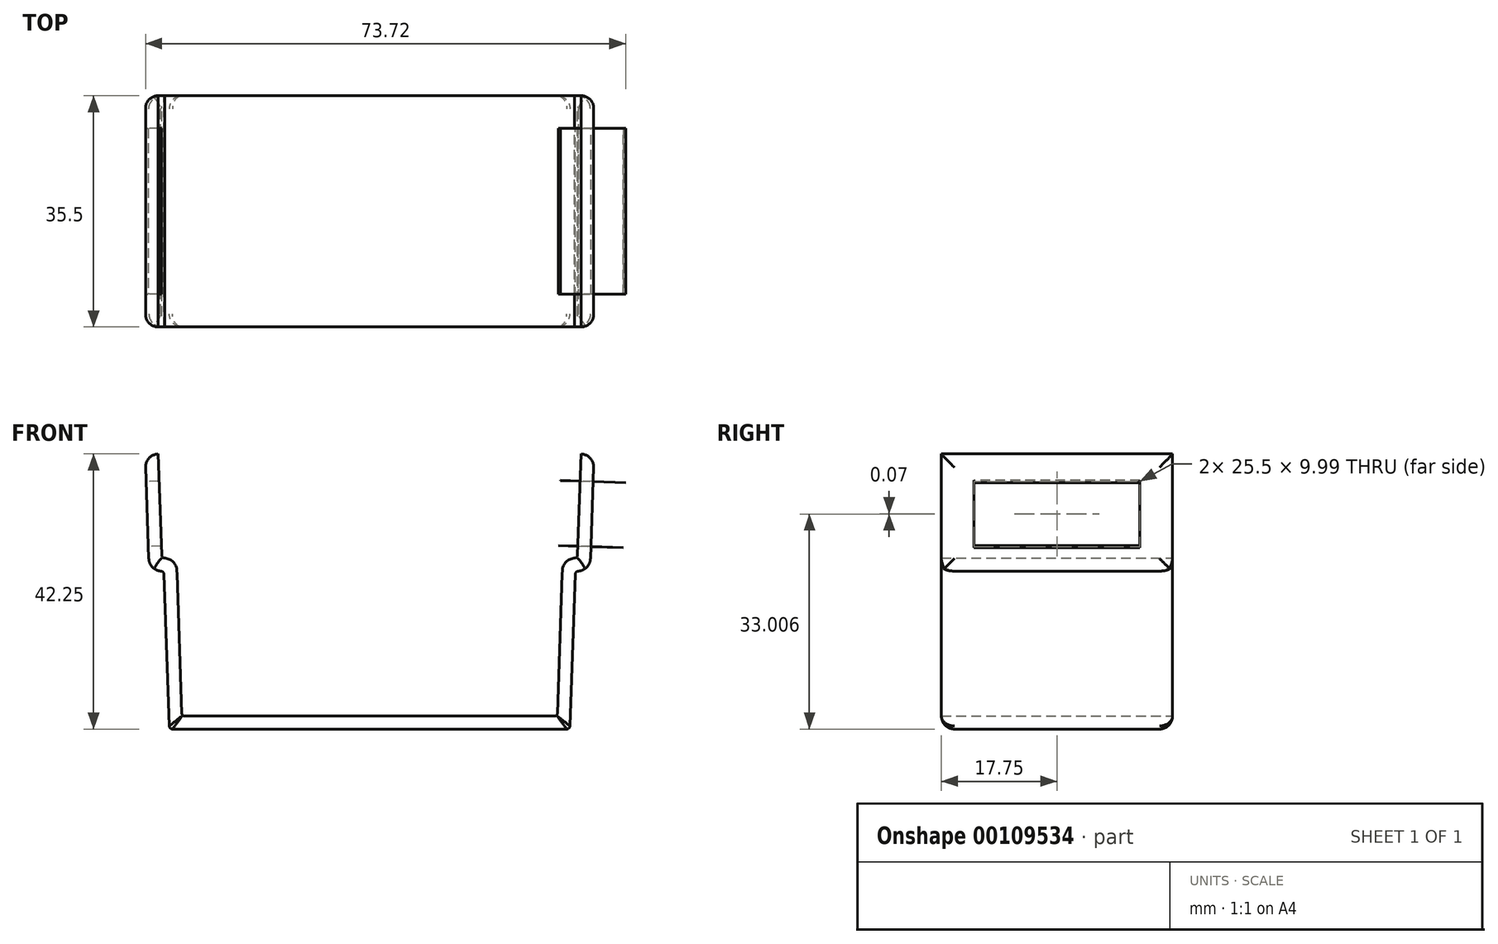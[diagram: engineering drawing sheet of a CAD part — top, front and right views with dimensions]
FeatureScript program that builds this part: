
annotation { "Feature Type Name" : "Feature", "Feature Type Description" : "" }
export const myFeature = defineFeature(function(context is Context, id is Id, definition is map)
    precondition{}
    {
        {
            var Q0;
            Q0=qCreatedBy(makeId("Front.planeOp"),FACE);
            var sketch = newSketch(context, id + "F0", { "sketchPlane" : qUnion([Q0])});
            skLineSegment(sketch, "E0", {"start": v(0, 0) * mm, "end": v(0, -5.67) * mm, "construction": true});
            skLineSegment(sketch, "E1", {"start": v(0, -5.67) * mm, "end": v(34.5, -5.67) * mm, "construction": true});
            skLineSegment(sketch, "E2", {"start": v(34.5, -5.67) * mm, "end": v(34.5, 0) * mm, "construction": true});
            skLineSegment(sketch, "E3.2", {"start": v(0, 2) * mm, "end": v(28.43, 2) * mm});
            skLineSegment(sketch, "E4.MirrorCS", {"start": v(-34.5, -5.67) * mm, "end": v(-34.5, 0) * mm, "construction": true});
            skLineSegment(sketch, "E5.MirrorCS", {"start": v(0, -5.67) * mm, "end": v(-34.5, -5.67) * mm, "construction": true});
            skLineSegment(sketch, "E6", {"start": v(29.6, 24.32) * mm, "end": v(28.83, 2.39) * mm});
            skLineSegment(sketch, "E7", {"start": v(30.77, 0.48) * mm, "end": v(31.58, 23.77) * mm});
            skLineSegment(sketch, "E8", {"start": v(0, 0) * mm, "end": v(30.27, 0) * mm});
            skLineSegment(sketch, "E9", {"start": v(32.23, 42.25) * mm, "end": v(57.13, 42.25) * mm, "construction": true});
            skLineSegment(sketch, "E10", {"start": v(57.13, 42.25) * mm, "end": v(57.13, 26.25) * mm, "construction": true});
            skLineSegment(sketch, "E11", {"start": v(57.13, 26.25) * mm, "end": v(31.92, 26.25) * mm, "construction": true});
            skLineSegment(sketch, "E12", {"start": v(32.08, 24.25) * mm, "end": v(31.92, 24.25) * mm});
            skLineSegment(sketch, "E13", {"start": v(33.91, 26.18) * mm, "end": v(34.48, 42.25) * mm});
            skLineSegment(sketch, "E14", {"start": v(31.43, 26.25) * mm, "end": v(31.6, 26.25) * mm});
            skLineSegment(sketch, "E15", {"start": v(31.93, 26.73) * mm, "end": v(32.47, 42.25) * mm});
            skLineSegment(sketch, "E16", {"start": v(32.47, 42.25) * mm, "end": v(34.48, 42.25) * mm});
            skLineSegment(sketch, "E17.trimOffspring", {"start": v(33.85, 24.25) * mm, "end": v(57.53, 24.25) * mm, "construction": true});
            skPoint(sketch, "E18.visualSharp", {"position": v(29.67, 26.25) * mm});
            skArc(sketch, "E18.filletArc", {"start": v(31.6, 26.25) * mm, "mid": v(30.2, 25.69) * mm, "end": v(29.6, 24.32) * mm});
            skArc(sketch, "E19.filletArc", {"start": v(32.08, 24.25) * mm, "mid": v(31.73, 24.1) * mm, "end": v(31.58, 23.77) * mm});
            skPoint(sketch, "E20.visualSharp", {"position": v(33.85, 24.25) * mm});
            skArc(sketch, "E20.filletArc", {"start": v(31.92, 24.25) * mm, "mid": v(33.3, 24.81) * mm, "end": v(33.91, 26.18) * mm});
            skArc(sketch, "E21.filletArc", {"start": v(31.43, 26.25) * mm, "mid": v(31.78, 26.4) * mm, "end": v(31.93, 26.73) * mm});
            skPoint(sketch, "E22.visualSharp", {"position": v(30.75, 0) * mm});
            skArc(sketch, "E22.filletArc", {"start": v(30.27, 0) * mm, "mid": v(30.61, 0.14) * mm, "end": v(30.77, 0.48) * mm});
            skPoint(sketch, "E23.visualSharp", {"position": v(28.82, 2) * mm});
            skArc(sketch, "E23.filletArc", {"start": v(28.43, 2) * mm, "mid": v(28.71, 2.11) * mm, "end": v(28.83, 2.39) * mm});
            skLineSegment(sketch, "E24.MirrorCS", {"start": v(-32.08, 24.25) * mm, "end": v(-31.92, 24.25) * mm});
            skArc(sketch, "E25.MirrorCS", {"start": v(-32.08, 24.25) * mm, "mid": v(-31.73, 24.1) * mm, "end": v(-31.58, 23.77) * mm});
            skArc(sketch, "E26.MirrorCS", {"start": v(-31.43, 26.25) * mm, "mid": v(-31.78, 26.4) * mm, "end": v(-31.93, 26.73) * mm});
            skArc(sketch, "E27.MirrorCS", {"start": v(-31.92, 24.25) * mm, "mid": v(-33.3, 24.81) * mm, "end": v(-33.91, 26.18) * mm});
            skLineSegment(sketch, "E28.MirrorCS", {"start": v(-31.43, 26.25) * mm, "end": v(-31.6, 26.25) * mm});
            skArc(sketch, "E29.MirrorCS", {"start": v(-28.43, 2) * mm, "mid": v(-28.71, 2.11) * mm, "end": v(-28.83, 2.39) * mm});
            skArc(sketch, "E30.MirrorCS", {"start": v(-30.27, 0) * mm, "mid": v(-30.61, 0.14) * mm, "end": v(-30.77, 0.48) * mm});
            skArc(sketch, "E31.MirrorCS", {"start": v(-31.6, 26.25) * mm, "mid": v(-30.2, 25.69) * mm, "end": v(-29.6, 24.32) * mm});
            skLineSegment(sketch, "E32.MirrorCS", {"start": v(-32.47, 42.25) * mm, "end": v(-34.48, 42.25) * mm});
            skLineSegment(sketch, "E33.MirrorCS", {"start": v(0, 0) * mm, "end": v(-30.27, 0) * mm});
            skLineSegment(sketch, "E34.MirrorCS", {"start": v(-30.77, 0.48) * mm, "end": v(-31.58, 23.77) * mm});
            skPoint(sketch, "E35.MirrorP", {"position": v(-29.67, 26.25) * mm});
            skPoint(sketch, "E36.MirrorP", {"position": v(-28.82, 2) * mm});
            skLineSegment(sketch, "E37.MirrorCS", {"start": v(0, 2) * mm, "end": v(-28.43, 2) * mm});
            skLineSegment(sketch, "E38.MirrorCS", {"start": v(-29.6, 24.32) * mm, "end": v(-28.83, 2.39) * mm});
            skLineSegment(sketch, "E39.MirrorCS", {"start": v(-31.93, 26.73) * mm, "end": v(-32.47, 42.25) * mm});
            skPoint(sketch, "E40.MirrorP", {"position": v(-33.85, 24.25) * mm});
            skLineSegment(sketch, "E41.MirrorCS", {"start": v(-33.91, 26.18) * mm, "end": v(-34.48, 42.25) * mm});
            skPoint(sketch, "E42.MirrorP", {"position": v(-30.75, 0) * mm});
            skLineSegment(sketch, "E43", {"start": v(32.23, 42.25) * mm, "end": v(27.53, 42.25) * mm, "construction": true});
            skSolve(sketch);
        }
        {
            var Q0;
            Q0 = qSketchRegion(id + "F0", true);
            extrude(context, id + "F1", {"entities" : qUnion([Q0]), "depth" : 35.5 * mm});
        }
        {
            var Q0;
            Q0=makeQuery(id+"F1.opExtrude","SWEPT_FACE",FACE,{"disambiguationData":[OSD([sQuery(id+"F0.wireOp",EDGE,"E13")])]});
            var sketch = newSketch(context, id + "F2", { "sketchPlane" : qUnion([Q0])});
            skLineSegment(sketch, "E44", {"start": v(-35.5, 43.43) * mm, "end": v(-35.5, 39.18) * mm, "construction": true});
            skLineSegment(sketch, "E45", {"start": v(-35.5, 39.18) * mm, "end": v(-35.5, 29.18) * mm, "construction": true});
            skLineSegment(sketch, "E46", {"start": v(-35.5, 43.43) * mm, "end": v(-30.5, 43.43) * mm, "construction": true});
            skLineSegment(sketch, "E47", {"start": v(0, 43.43) * mm, "end": v(-5, 43.43) * mm, "construction": true});
            skLineSegment(sketch, "E48", {"start": v(-30.5, 39.18) * mm, "end": v(-5, 39.18) * mm});
            skLineSegment(sketch, "E49", {"start": v(-30.5, 39.18) * mm, "end": v(-30.5, 29.18) * mm});
            skLineSegment(sketch, "E50", {"start": v(-5, 39.18) * mm, "end": v(-5, 29.18) * mm});
            skLineSegment(sketch, "E51", {"start": v(-30.5, 29.18) * mm, "end": v(-5, 29.18) * mm});
            skLineSegment(sketch, "E52", {"start": v(-5, 43.43) * mm, "end": v(-5, 39.18) * mm, "construction": true});
            skLineSegment(sketch, "E53", {"start": v(-30.5, 43.43) * mm, "end": v(-30.5, 39.18) * mm, "construction": true});
            skSolve(sketch);
        }
        {
            var Q0;
            Q0 = qSketchRegion(id + "F2", true);
            extrude(context, id + "F3", {"entities" : qUnion([Q0]), "operationType" : NewBodyOperationType.REMOVE, "oppositeDirection" : true, "depth" : 5 * mm});
        }
        {
            var Q0;
            Q0=makeQuery(id+"F1.opExtrude","SWEPT_FACE",FACE,{"disambiguationData":[OSD([sQuery(id+"F0.wireOp",EDGE,"E41.MirrorCS")])]});
            var sketch = newSketch(context, id + "F4", { "sketchPlane" : qUnion([Q0])});
            skLineSegment(sketch, "E54", {"start": v(0, 39.18) * mm, "end": v(0, 29.18) * mm, "construction": true});
            skLineSegment(sketch, "E55", {"start": v(5, 39.18) * mm, "end": v(30.5, 39.18) * mm});
            skLineSegment(sketch, "E56", {"start": v(30.5, 39.18) * mm, "end": v(30.5, 29.18) * mm});
            skLineSegment(sketch, "E57", {"start": v(5, 29.18) * mm, "end": v(30.5, 29.18) * mm});
            skLineSegment(sketch, "E58", {"start": v(0, 43.43) * mm, "end": v(5, 43.43) * mm, "construction": true});
            skLineSegment(sketch, "E59", {"start": v(5, 39.18) * mm, "end": v(5, 29.18) * mm});
            skLineSegment(sketch, "E60", {"start": v(5, 43.43) * mm, "end": v(5, 39.18) * mm, "construction": true});
            skLineSegment(sketch, "E61", {"start": v(30.5, 43.43) * mm, "end": v(30.5, 39.18) * mm, "construction": true});
            skLineSegment(sketch, "E62", {"start": v(35.5, 43.43) * mm, "end": v(30.5, 43.43) * mm, "construction": true});
            skSolve(sketch);
        }
        {
            var Q0;
            Q0 = qSketchRegion(id + "F4", true);
            extrude(context, id + "F5", {"entities" : qUnion([Q0]), "operationType" : NewBodyOperationType.REMOVE, "oppositeDirection" : true, "depth" : 5 * mm});
        }
        {
            var Q0;
            Q0=makeQuery(id+"F1.opExtrude","CAP_EDGE",EDGE,{"disambiguationData":[OSD([sQuery(id+"F0.wireOp",EDGE,"E34.MirrorCS")])],"isStart":false});
            var Q1;
            Q1=makeQuery(id+"F1.opExtrude","CAP_EDGE",EDGE,{"disambiguationData":[OSD([sQuery(id+"F0.wireOp",EDGE,"E34.MirrorCS")])],"isStart":true});
            fillet(context, id + "F6", {"entities" : qUnion([Q0, Q1]), "radius" : 2 * mm, "tangentPropagation" : true, "allowEdgeOverflow" : false});
        }
        {
            var Q0;
            Q0=makeQuery(id+"F1.opExtrude","CAP_EDGE",EDGE,{"disambiguationData":[OSD([sQuery(id+"F0.wireOp",EDGE,"E41.MirrorCS")])],"isStart":false});
            var Q1;
            Q1=makeQuery(id+"F1.opExtrude","CAP_EDGE",EDGE,{"disambiguationData":[OSD([sQuery(id+"F0.wireOp",EDGE,"E41.MirrorCS")])],"isStart":true});
            var Q2;
            Q2=makeQuery(id+"F1.opExtrude","CAP_EDGE",EDGE,{"disambiguationData":[OSD([sQuery(id+"F0.wireOp",EDGE,"E13")])],"isStart":false});
            var Q3;
            Q3=makeQuery(id+"F1.opExtrude","CAP_EDGE",EDGE,{"disambiguationData":[OSD([sQuery(id+"F0.wireOp",EDGE,"E13")])],"isStart":true});
            var Q4;
            Q4=makeQuery(id+"F1.opExtrude","SWEPT_EDGE",EDGE,{"disambiguationData":[OSD([sQuery(id+"F0.wireOp",EDGE,"E13"),sQuery(id+"F0.wireOp",EDGE,"E16")])]});
            var Q5;
            Q5=makeQuery(id+"F1.opExtrude","SWEPT_EDGE",EDGE,{"disambiguationData":[OSD([sQuery(id+"F0.wireOp",EDGE,"E32.MirrorCS"),sQuery(id+"F0.wireOp",EDGE,"E41.MirrorCS")])]});
            fillet(context, id + "F7", {"entities" : qUnion([Q0, Q1, Q2, Q3, Q4, Q5]), "radius" : 2 * mm, "tangentPropagation" : true, "allowEdgeOverflow" : false});
        }
        {
            var Q0;
            Q0=makeQuery(id+"F1.opExtrude","SWEPT_FACE",FACE,{"disambiguationData":[OSD([sQuery(id+"F0.wireOp",EDGE,"E13")])]});
            var sketch = newSketch(context, id + "F8", { "sketchPlane" : qUnion([Q0])});
            skLineSegment(sketch, "E63", {"start": v(-5, 39.19) * mm, "end": v(-30.5, 39.19) * mm});
            skLineSegment(sketch, "E64", {"start": v(-30.5, 38.25) * mm, "end": v(-30.5, 39.19) * mm});
            skLineSegment(sketch, "E65", {"start": v(-5, 29.18) * mm, "end": v(-5, 29.17) * mm});
            skLineSegment(sketch, "E66", {"start": v(-5, 29.17) * mm, "end": v(-30.5, 29.17) * mm});
            skLineSegment(sketch, "E67", {"start": v(-30.5, 29.18) * mm, "end": v(-30.5, 29.19) * mm});
            skLineSegment(sketch, "E68", {"start": v(-30.5, 29.19) * mm, "end": v(-5, 29.19) * mm});
            skLineSegment(sketch, "E69", {"start": v(-5, 29.19) * mm, "end": v(-5, 29.18) * mm});
            skLineSegment(sketch, "E70", {"start": v(-30.5, 29.18) * mm, "end": v(-30.5, 29.17) * mm});
            skLineSegment(sketch, "E71", {"start": v(-5, 39.17) * mm, "end": v(-30.5, 39.17) * mm});
            skLineSegment(sketch, "E72", {"start": v(-30.5, 39.17) * mm, "end": v(-30.5, 38.25) * mm});
            skLineSegment(sketch, "E73", {"start": v(-5, 39.19) * mm, "end": v(-5, 39.17) * mm});
            skSolve(sketch);
        }
        {
            var Q0;
            Q0 = qSketchRegion(id + "F8", true);
            extrude(context, id + "F9", {"entities" : qUnion([Q0]), "depth" : 5 * mm, "hasSecondDirection" : true, "secondDirectionOppositeDirection" : true, "secondDirectionDepth" : 5 * mm});
        }
    });
